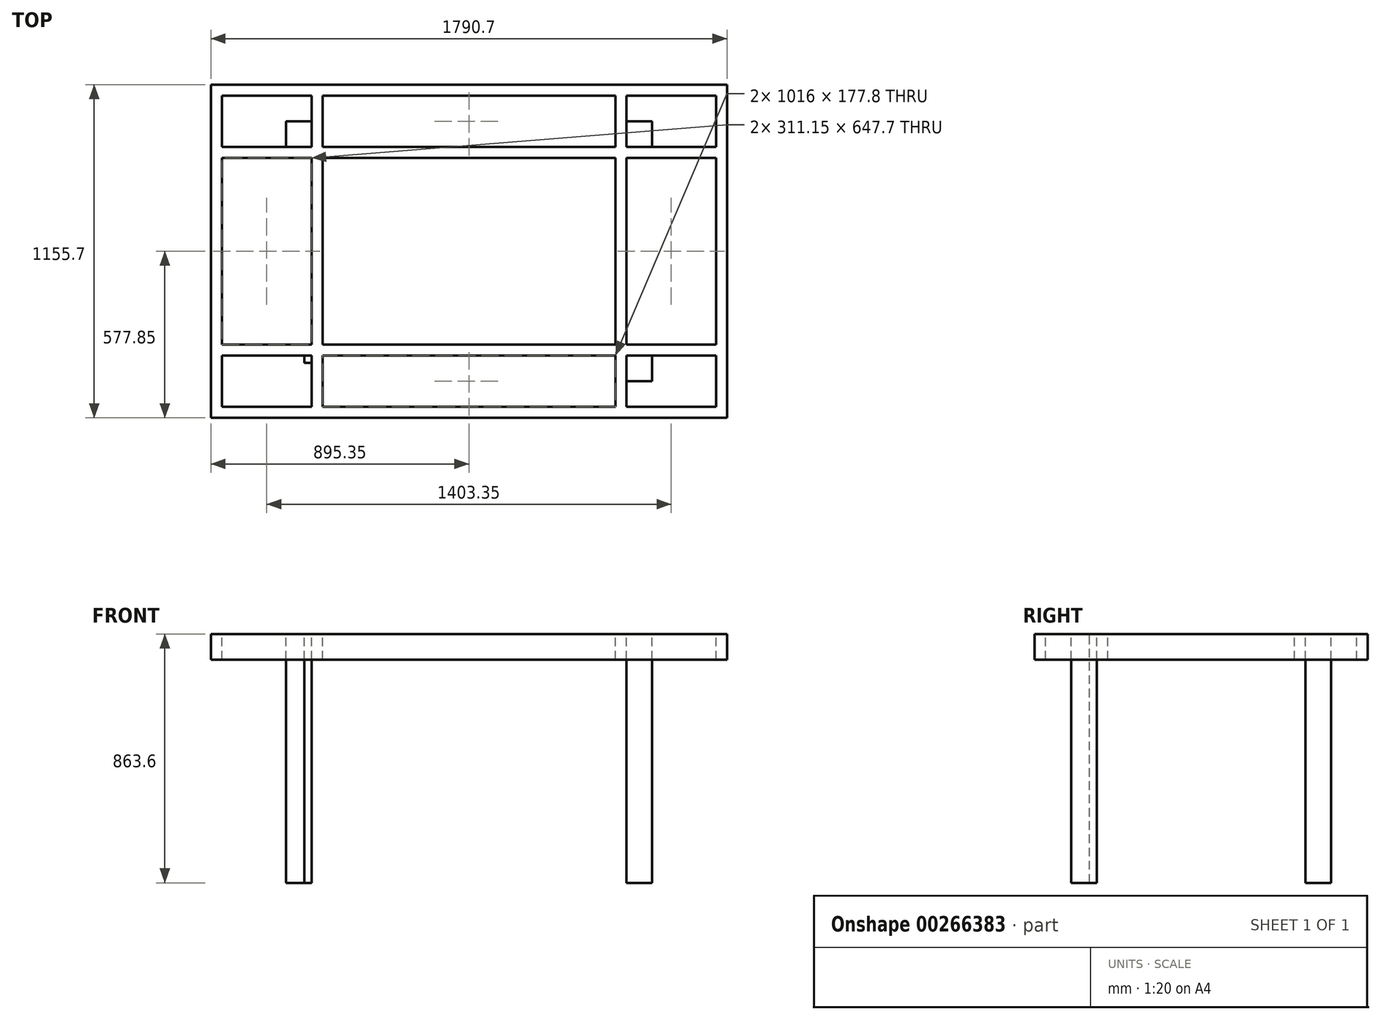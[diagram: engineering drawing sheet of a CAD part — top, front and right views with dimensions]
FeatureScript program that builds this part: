
annotation { "Feature Type Name" : "Feature", "Feature Type Description" : "" }
export const myFeature = defineFeature(function(context is Context, id is Id, definition is map)
    precondition{}
    {
        {
            var Q0;
            Q0=qCreatedBy(makeId("Top.planeOp"),FACE);
            var sketch = newSketch(context, id + "F0", { "sketchPlane" : qUnion([Q0])});
            skLineSegment(sketch, "E0.bottom", {"start": v(508, 323.85) * mm, "end": v(-508, 323.85) * mm});
            skLineSegment(sketch, "E0.top", {"start": v(508, -323.85) * mm, "end": v(-508, -323.85) * mm});
            skLineSegment(sketch, "E0.left", {"start": v(508, 323.85) * mm, "end": v(508, -323.85) * mm});
            skLineSegment(sketch, "E0.right", {"start": v(-508, 323.85) * mm, "end": v(-508, -323.85) * mm});
            skPoint(sketch, "E0.middle", {"position": v(0, 0) * mm});
            skLineSegment(sketch, "E1.bottom", {"start": v(-546.1, -361.95) * mm, "end": v(546.1, -361.95) * mm});
            skLineSegment(sketch, "E1.top", {"start": v(-546.1, 361.95) * mm, "end": v(546.1, 361.95) * mm});
            skLineSegment(sketch, "E1.left", {"start": v(-546.1, -361.95) * mm, "end": v(-546.1, 361.95) * mm});
            skLineSegment(sketch, "E1.right", {"start": v(546.1, -361.95) * mm, "end": v(546.1, 361.95) * mm});
            skLineSegment(sketch, "E2.bottom", {"start": v(-895.35, 577.85) * mm, "end": v(895.35, 577.85) * mm});
            skLineSegment(sketch, "E2.top", {"start": v(-895.35, -577.85) * mm, "end": v(895.35, -577.85) * mm});
            skLineSegment(sketch, "E2.left", {"start": v(-895.35, 577.85) * mm, "end": v(-895.35, -577.85) * mm});
            skLineSegment(sketch, "E2.right", {"start": v(895.35, 577.85) * mm, "end": v(895.35, -577.85) * mm});
            skLineSegment(sketch, "E3.bottom", {"start": v(-857.25, -539.75) * mm, "end": v(857.25, -539.75) * mm});
            skLineSegment(sketch, "E3.top", {"start": v(-857.25, 539.75) * mm, "end": v(857.25, 539.75) * mm});
            skLineSegment(sketch, "E3.left", {"start": v(-857.25, -539.75) * mm, "end": v(-857.25, 539.75) * mm});
            skLineSegment(sketch, "E3.right", {"start": v(857.25, -539.75) * mm, "end": v(857.25, 539.75) * mm});
            skLineSegment(sketch, "E4", {"start": v(-546.1, 361.95) * mm, "end": v(-895.35, 361.95) * mm});
            skLineSegment(sketch, "E5", {"start": v(-508, 323.85) * mm, "end": v(-895.35, 323.85) * mm});
            skLineSegment(sketch, "E6", {"start": v(-546.1, 361.95) * mm, "end": v(-546.1, 577.85) * mm});
            skLineSegment(sketch, "E7", {"start": v(-508, 323.85) * mm, "end": v(-508, 577.85) * mm});
            skLineSegment(sketch, "E8", {"start": v(546.1, 361.95) * mm, "end": v(546.1, 577.85) * mm});
            skLineSegment(sketch, "E9", {"start": v(508, 323.85) * mm, "end": v(508, 577.85) * mm});
            skLineSegment(sketch, "E10", {"start": v(508, -323.85) * mm, "end": v(508, -577.85) * mm});
            skLineSegment(sketch, "E11", {"start": v(546.1, -361.95) * mm, "end": v(546.1, -577.85) * mm});
            skLineSegment(sketch, "E12", {"start": v(546.1, -361.95) * mm, "end": v(895.35, -361.95) * mm});
            skLineSegment(sketch, "E13", {"start": v(508, -323.85) * mm, "end": v(895.35, -323.85) * mm});
            skLineSegment(sketch, "E14", {"start": v(-546.1, -361.95) * mm, "end": v(-895.35, -361.95) * mm});
            skLineSegment(sketch, "E15", {"start": v(-508, -323.85) * mm, "end": v(-895.35, -323.85) * mm});
            skLineSegment(sketch, "E16", {"start": v(546.1, 361.95) * mm, "end": v(895.35, 361.95) * mm});
            skLineSegment(sketch, "E17", {"start": v(508, 323.85) * mm, "end": v(895.35, 323.85) * mm});
            skLineSegment(sketch, "E18", {"start": v(-546.1, -361.95) * mm, "end": v(-546.1, -577.85) * mm});
            skLineSegment(sketch, "E19", {"start": v(-508, -323.85) * mm, "end": v(-508, -577.85) * mm});
            skSolve(sketch);
        }
        {
            var Q0;
            Q0=qSketchRegion(id+"F0",true);
            var Q1;
            {var subQ3=sQuery(id+"F0.wireOp",EDGE,"E5");var subQ5=sQuery(id+"F0.wireOp",EDGE,"E3.left");var subQ6=makeQuery(id+"F0.imprint","INTERSECT",VERTEX,{"derivedFrom":[subQ5,subQ3]});Q1=makeQuery(id+"F0.imprint","IMPRINT",FACE,{"disambiguationData":[TD([[makeQuery(id+"F0.imprint","IMPRINT",EDGE,{"disambiguationData":[TD([[subQ6,-1.0]])],"derivedFrom":subQ5}),-1.0]])]});}
            var Q2;
            {var subQ0=sQuery(id+"F0.wireOp",EDGE,"E6");var subQ5=sQuery(id+"F0.wireOp",EDGE,"E3.top");var subQ7=makeQuery(id+"F0.imprint","INTERSECT",VERTEX,{"derivedFrom":[subQ5,subQ0]});Q2=makeQuery(id+"F0.imprint","IMPRINT",FACE,{"disambiguationData":[TD([[makeQuery(id+"F0.imprint","IMPRINT",EDGE,{"disambiguationData":[TD([[subQ7,-1.0]])],"derivedFrom":subQ5}),-1.0]])]});}
            var Q3;
            {var subQ1=sQuery(id+"F0.wireOp",EDGE,"E1.top");var subQ3=sQuery(id+"F0.wireOp",EDGE,"E7");var subQ4=makeQuery(id+"F0.imprint","INTERSECT",VERTEX,{"derivedFrom":[subQ1,subQ3]});Q3=makeQuery(id+"F0.imprint","IMPRINT",FACE,{"disambiguationData":[TD([[makeQuery(id+"F0.imprint","IMPRINT",EDGE,{"disambiguationData":[TD([[subQ4,1.0]])],"derivedFrom":subQ1}),-1.0]])]});}
            var Q4;
            {var subQ0=sQuery(id+"F0.wireOp",EDGE,"E0.right");Q4=makeQuery(id+"F0.imprint","IMPRINT",FACE,{"disambiguationData":[TD([[makeQuery(id+"F0.imprint","IMPRINT",EDGE,{"derivedFrom":subQ0}),-1.0]])]});}
            var Q5;
            {var subQ0=sQuery(id+"F0.wireOp",EDGE,"E14");var subQ5=sQuery(id+"F0.wireOp",EDGE,"E3.left");var subQ6=makeQuery(id+"F0.imprint","INTERSECT",VERTEX,{"derivedFrom":[subQ5,subQ0]});Q5=makeQuery(id+"F0.imprint","IMPRINT",FACE,{"disambiguationData":[TD([[makeQuery(id+"F0.imprint","IMPRINT",EDGE,{"disambiguationData":[TD([[subQ6,-1.0]])],"derivedFrom":subQ5}),-1.0]])]});}
            var Q6;
            {var subQ0=sQuery(id+"F0.wireOp",EDGE,"E18");var subQ5=sQuery(id+"F0.wireOp",EDGE,"E3.bottom");var subQ6=makeQuery(id+"F0.imprint","INTERSECT",VERTEX,{"derivedFrom":[subQ5,subQ0]});Q6=makeQuery(id+"F0.imprint","IMPRINT",FACE,{"disambiguationData":[TD([[makeQuery(id+"F0.imprint","IMPRINT",EDGE,{"disambiguationData":[TD([[subQ6,-1.0]])],"derivedFrom":subQ5}),1.0]])]});}
            var Q7;
            {var subQ1=sQuery(id+"F0.wireOp",EDGE,"E1.bottom");var subQ3=sQuery(id+"F0.wireOp",EDGE,"E19");var subQ4=makeQuery(id+"F0.imprint","INTERSECT",VERTEX,{"derivedFrom":[subQ1,subQ3]});Q7=makeQuery(id+"F0.imprint","IMPRINT",FACE,{"disambiguationData":[TD([[makeQuery(id+"F0.imprint","IMPRINT",EDGE,{"disambiguationData":[TD([[subQ4,1.0]])],"derivedFrom":subQ1}),1.0]])]});}
            var Q8;
            {var subQ0=sQuery(id+"F0.wireOp",EDGE,"E0.top");Q8=makeQuery(id+"F0.imprint","IMPRINT",FACE,{"disambiguationData":[TD([[makeQuery(id+"F0.imprint","IMPRINT",EDGE,{"derivedFrom":subQ0}),1.0]])]});}
            var Q9;
            {var subQ3=sQuery(id+"F0.wireOp",EDGE,"E10");var subQ5=sQuery(id+"F0.wireOp",EDGE,"E3.bottom");var subQ6=makeQuery(id+"F0.imprint","INTERSECT",VERTEX,{"derivedFrom":[subQ5,subQ3]});Q9=makeQuery(id+"F0.imprint","IMPRINT",FACE,{"disambiguationData":[TD([[makeQuery(id+"F0.imprint","IMPRINT",EDGE,{"disambiguationData":[TD([[subQ6,-1.0]])],"derivedFrom":subQ5}),1.0]])]});}
            var Q10;
            {var subQ1=sQuery(id+"F0.wireOp",EDGE,"E1.bottom");var subQ3=sQuery(id+"F0.wireOp",EDGE,"E10");var subQ4=makeQuery(id+"F0.imprint","INTERSECT",VERTEX,{"derivedFrom":[subQ1,subQ3]});Q10=makeQuery(id+"F0.imprint","IMPRINT",FACE,{"disambiguationData":[TD([[makeQuery(id+"F0.imprint","IMPRINT",EDGE,{"disambiguationData":[TD([[subQ4,-1.0]])],"derivedFrom":subQ1}),1.0]])]});}
            var Q11;
            {var subQ0=sQuery(id+"F0.wireOp",EDGE,"E12");var subQ5=sQuery(id+"F0.wireOp",EDGE,"E3.right");var subQ6=makeQuery(id+"F0.imprint","INTERSECT",VERTEX,{"derivedFrom":[subQ5,subQ0]});Q11=makeQuery(id+"F0.imprint","IMPRINT",FACE,{"disambiguationData":[TD([[makeQuery(id+"F0.imprint","IMPRINT",EDGE,{"disambiguationData":[TD([[subQ6,-1.0]])],"derivedFrom":subQ5}),1.0]])]});}
            var Q12;
            {var subQ0=sQuery(id+"F0.wireOp",EDGE,"E0.left");Q12=makeQuery(id+"F0.imprint","IMPRINT",FACE,{"disambiguationData":[TD([[makeQuery(id+"F0.imprint","IMPRINT",EDGE,{"derivedFrom":subQ0}),1.0]])]});}
            var Q13;
            {var subQ1=sQuery(id+"F0.wireOp",EDGE,"E1.top");var subQ3=sQuery(id+"F0.wireOp",EDGE,"E9");var subQ4=makeQuery(id+"F0.imprint","INTERSECT",VERTEX,{"derivedFrom":[subQ1,subQ3]});Q13=makeQuery(id+"F0.imprint","IMPRINT",FACE,{"disambiguationData":[TD([[makeQuery(id+"F0.imprint","IMPRINT",EDGE,{"disambiguationData":[TD([[subQ4,-1.0]])],"derivedFrom":subQ1}),-1.0]])]});}
            var Q14;
            {var subQ3=sQuery(id+"F0.wireOp",EDGE,"E9");var subQ5=sQuery(id+"F0.wireOp",EDGE,"E3.top");var subQ6=makeQuery(id+"F0.imprint","INTERSECT",VERTEX,{"derivedFrom":[subQ5,subQ3]});Q14=makeQuery(id+"F0.imprint","IMPRINT",FACE,{"disambiguationData":[TD([[makeQuery(id+"F0.imprint","IMPRINT",EDGE,{"disambiguationData":[TD([[subQ6,-1.0]])],"derivedFrom":subQ5}),-1.0]])]});}
            var Q15;
            {var subQ3=sQuery(id+"F0.wireOp",EDGE,"E17");var subQ5=sQuery(id+"F0.wireOp",EDGE,"E3.right");var subQ6=makeQuery(id+"F0.imprint","INTERSECT",VERTEX,{"derivedFrom":[subQ5,subQ3]});Q15=makeQuery(id+"F0.imprint","IMPRINT",FACE,{"disambiguationData":[TD([[makeQuery(id+"F0.imprint","IMPRINT",EDGE,{"disambiguationData":[TD([[subQ6,-1.0]])],"derivedFrom":subQ5}),1.0]])]});}
            var Q16;
            {var subQ0=sQuery(id+"F0.wireOp",EDGE,"E0.bottom");Q16=makeQuery(id+"F0.imprint","IMPRINT",FACE,{"disambiguationData":[TD([[makeQuery(id+"F0.imprint","IMPRINT",EDGE,{"derivedFrom":subQ0}),-1.0]])]});}
            extrude(context, id + "F1", {"entities" : qUnion([Q0, Q1, Q2, Q3, Q4, Q5, Q6, Q7, Q8, Q9, Q10, Q11, Q12, Q13, Q14, Q15, Q16]), "oppositeDirection" : true, "depth" : 88.9 * mm});
        }
        {
            var Q0;
            Q0=makeQuery(id+"F1.opExtrude","CAP_FACE",FACE,{"disambiguationData":[OSD([sQuery(id+"F0.wireOp",EDGE,"E0.bottom"),sQuery(id+"F0.wireOp",EDGE,"E0.top"),sQuery(id+"F0.wireOp",EDGE,"E0.left"),sQuery(id+"F0.wireOp",EDGE,"E0.right"),sQuery(id+"F0.wireOp",EDGE,"E1.bottom"),sQuery(id+"F0.wireOp",EDGE,"E1.top"),sQuery(id+"F0.wireOp",EDGE,"E1.left"),sQuery(id+"F0.wireOp",EDGE,"E1.right"),sQuery(id+"F0.wireOp",EDGE,"E2.bottom"),sQuery(id+"F0.wireOp",EDGE,"E2.top"),sQuery(id+"F0.wireOp",EDGE,"E2.left"),sQuery(id+"F0.wireOp",EDGE,"E2.right"),sQuery(id+"F0.wireOp",EDGE,"E3.bottom"),sQuery(id+"F0.wireOp",EDGE,"E3.top"),sQuery(id+"F0.wireOp",EDGE,"E3.left"),sQuery(id+"F0.wireOp",EDGE,"E3.right"),sQuery(id+"F0.wireOp",EDGE,"E4"),sQuery(id+"F0.wireOp",EDGE,"E5"),sQuery(id+"F0.wireOp",EDGE,"E6"),sQuery(id+"F0.wireOp",EDGE,"E7"),sQuery(id+"F0.wireOp",EDGE,"E8"),sQuery(id+"F0.wireOp",EDGE,"E9"),sQuery(id+"F0.wireOp",EDGE,"E10"),sQuery(id+"F0.wireOp",EDGE,"E11"),sQuery(id+"F0.wireOp",EDGE,"E12"),sQuery(id+"F0.wireOp",EDGE,"E13"),sQuery(id+"F0.wireOp",EDGE,"E14"),sQuery(id+"F0.wireOp",EDGE,"E15"),sQuery(id+"F0.wireOp",EDGE,"E16"),sQuery(id+"F0.wireOp",EDGE,"E17"),sQuery(id+"F0.wireOp",EDGE,"E18"),sQuery(id+"F0.wireOp",EDGE,"E19")])],"isStart":true});
            var sketch = newSketch(context, id + "F2", { "sketchPlane" : qUnion([Q0])});
            skLineSegment(sketch, "E20.bottom", {"start": v(-546.1, -361.95) * mm, "end": v(-635, -361.95) * mm});
            skLineSegment(sketch, "E20.top", {"start": v(-546.1, -450.85) * mm, "end": v(-635, -450.85) * mm});
            skLineSegment(sketch, "E20.left", {"start": v(-546.1, -361.95) * mm, "end": v(-546.1, -450.85) * mm});
            skLineSegment(sketch, "E20.right", {"start": v(-635, -361.95) * mm, "end": v(-635, -450.85) * mm});
            skLineSegment(sketch, "E21.bottom", {"start": v(546.1, -361.95) * mm, "end": v(635, -361.95) * mm});
            skLineSegment(sketch, "E21.top", {"start": v(546.1, -450.85) * mm, "end": v(635, -450.85) * mm});
            skLineSegment(sketch, "E21.left", {"start": v(546.1, -361.95) * mm, "end": v(546.1, -450.85) * mm});
            skLineSegment(sketch, "E21.right", {"start": v(635, -361.95) * mm, "end": v(635, -450.85) * mm});
            skLineSegment(sketch, "E22.bottom", {"start": v(546.1, 361.95) * mm, "end": v(635, 361.95) * mm});
            skLineSegment(sketch, "E22.top", {"start": v(546.1, 450.85) * mm, "end": v(635, 450.85) * mm});
            skLineSegment(sketch, "E22.left", {"start": v(546.1, 361.95) * mm, "end": v(546.1, 450.85) * mm});
            skLineSegment(sketch, "E22.right", {"start": v(635, 361.95) * mm, "end": v(635, 450.85) * mm});
            skLineSegment(sketch, "E23.bottom", {"start": v(-546.1, 361.95) * mm, "end": v(-635, 361.95) * mm});
            skLineSegment(sketch, "E23.top", {"start": v(-546.1, 450.85) * mm, "end": v(-635, 450.85) * mm});
            skLineSegment(sketch, "E23.left", {"start": v(-546.1, 361.95) * mm, "end": v(-546.1, 450.85) * mm});
            skLineSegment(sketch, "E23.right", {"start": v(-635, 361.95) * mm, "end": v(-635, 450.85) * mm});
            skLineSegment(sketch, "E24.bottom", {"start": v(-546.1, -361.95) * mm, "end": v(-571.5, -361.95) * mm});
            skLineSegment(sketch, "E24.top", {"start": v(-546.1, -387.35) * mm, "end": v(-571.5, -387.35) * mm});
            skLineSegment(sketch, "E24.left", {"start": v(-546.1, -361.95) * mm, "end": v(-546.1, -387.35) * mm});
            skLineSegment(sketch, "E24.right", {"start": v(-571.5, -361.95) * mm, "end": v(-571.5, -387.35) * mm});
            skSolve(sketch);
        }
        {
            var Q0;
            Q0=makeQuery(id+"F2.imprint","IMPRINT",FACE,{"disambiguationData":[TD([[makeQuery(id+"F2.imprint","IMPRINT",EDGE,{"derivedFrom":sQuery(id+"F2.wireOp",EDGE,"E20.bottom")}),1.0]])]});
            var Q1;
            Q1=makeQuery(id+"F2.imprint","IMPRINT",FACE,{"disambiguationData":[TD([[makeQuery(id+"F2.imprint","IMPRINT",EDGE,{"derivedFrom":sQuery(id+"F2.wireOp",EDGE,"E21.bottom")}),-1.0]])]});
            var Q2;
            Q2=makeQuery(id+"F2.imprint","IMPRINT",FACE,{"disambiguationData":[TD([[makeQuery(id+"F2.imprint","IMPRINT",EDGE,{"derivedFrom":sQuery(id+"F2.wireOp",EDGE,"E22.bottom")}),1.0]])]});
            var Q3;
            Q3=makeQuery(id+"F2.imprint","IMPRINT",FACE,{"disambiguationData":[TD([[makeQuery(id+"F2.imprint","IMPRINT",EDGE,{"derivedFrom":sQuery(id+"F2.wireOp",EDGE,"E23.bottom")}),-1.0]])]});
            extrude(context, id + "F3", {"entities" : qUnion([Q0, Q1, Q2, Q3]), "oppositeDirection" : true, "depth" : 863.6 * mm});
        }
    });
